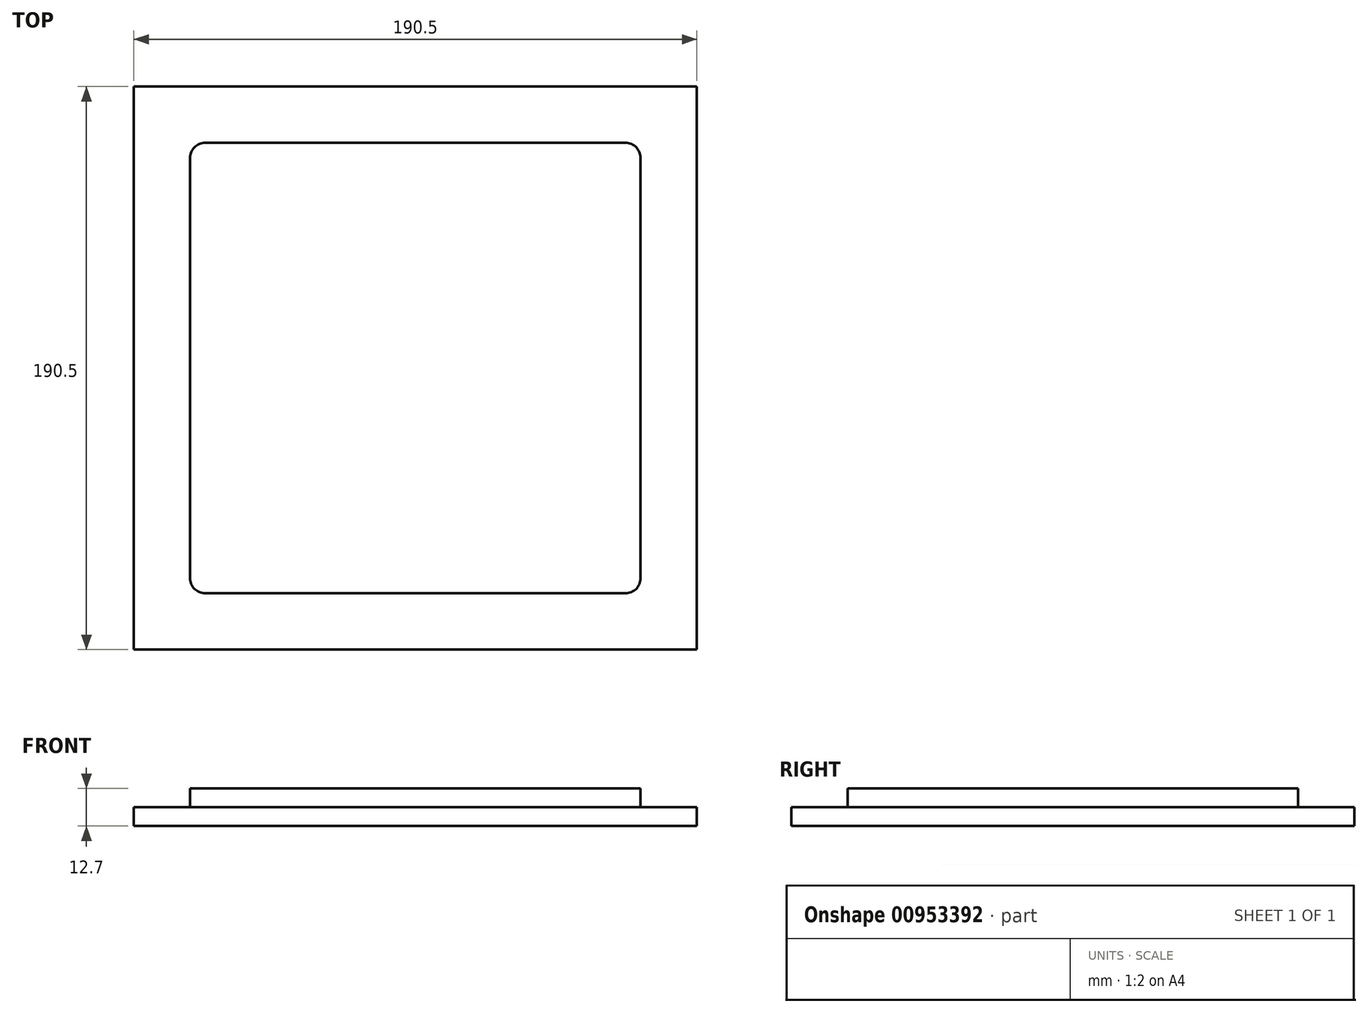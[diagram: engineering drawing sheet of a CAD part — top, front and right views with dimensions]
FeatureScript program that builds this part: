
annotation { "Feature Type Name" : "Feature", "Feature Type Description" : "" }
export const myFeature = defineFeature(function(context is Context, id is Id, definition is map)
    precondition{}
    {
        {
            var Q0;
            Q0=qCreatedBy(makeId("Top.planeOp"),FACE);
            var sketch = newSketch(context, id + "F0", { "sketchPlane" : qUnion([Q0])});
            skLineSegment(sketch, "E0.bottom", {"start": v(-95.25, 95.25) * mm, "end": v(95.25, 95.25) * mm});
            skLineSegment(sketch, "E0.top", {"start": v(-95.25, -95.25) * mm, "end": v(95.25, -95.25) * mm});
            skLineSegment(sketch, "E0.left", {"start": v(-95.25, 95.25) * mm, "end": v(-95.25, -95.25) * mm});
            skLineSegment(sketch, "E0.right", {"start": v(95.25, 95.25) * mm, "end": v(95.25, -95.25) * mm});
            skPoint(sketch, "E0.middle", {"position": v(0, 0) * mm});
            skSolve(sketch);
        }
        {
            var Q0;
            Q0=makeQuery(id+"F0.imprint","IMPRINT",FACE,{"disambiguationData":[TD([[makeQuery(id+"F0.imprint","IMPRINT",EDGE,{"derivedFrom":sQuery(id+"F0.wireOp",EDGE,"E0.bottom")}),-1.0]])]});
            extrude(context, id + "F1", {"entities" : qUnion([Q0]), "depth" : 6.35 * mm, "offsetDistance" : 25.4 * mm});
        }
        {
            var Q0;
            Q0=makeQuery(id+"F1.opExtrude","CAP_FACE",FACE,{"disambiguationData":[OSD([sQuery(id+"F0.wireOp",EDGE,"E0.bottom"),sQuery(id+"F0.wireOp",EDGE,"E0.top"),sQuery(id+"F0.wireOp",EDGE,"E0.left"),sQuery(id+"F0.wireOp",EDGE,"E0.right")])],"isStart":false});
            var sketch = newSketch(context, id + "F2", { "sketchPlane" : qUnion([Q0])});
            skLineSegment(sketch, "E1.bottom", {"start": v(-76.2, 76.2) * mm, "end": v(76.2, 76.2) * mm});
            skLineSegment(sketch, "E1.top", {"start": v(-76.2, -76.2) * mm, "end": v(76.2, -76.2) * mm});
            skLineSegment(sketch, "E1.left", {"start": v(-76.2, 76.2) * mm, "end": v(-76.2, -76.2) * mm});
            skLineSegment(sketch, "E1.right", {"start": v(76.2, 76.2) * mm, "end": v(76.2, -76.2) * mm});
            skPoint(sketch, "E1.middle", {"position": v(0, 0) * mm});
            skSolve(sketch);
        }
        {
            var Q0;
            Q0=makeQuery(id+"F2.imprint","IMPRINT",FACE,{"disambiguationData":[TD([[makeQuery(id+"F2.imprint","IMPRINT",EDGE,{"derivedFrom":sQuery(id+"F2.wireOp",EDGE,"E1.bottom")}),-1.0]])]});
            extrude(context, id + "F3", {"entities" : qUnion([Q0]), "depth" : 6.35 * mm, "offsetDistance" : 25.4 * mm});
        }
        {
            var Q0;
            Q0=makeQuery(id+"F3.opExtrude","SWEPT_EDGE",EDGE,{"disambiguationData":[OSD([sQuery(id+"F2.wireOp",EDGE,"E1.top"),sQuery(id+"F2.wireOp",EDGE,"E1.right")])]});
            var Q1;
            Q1=makeQuery(id+"F3.opExtrude","SWEPT_EDGE",EDGE,{"disambiguationData":[OSD([sQuery(id+"F2.wireOp",EDGE,"E1.top"),sQuery(id+"F2.wireOp",EDGE,"E1.left")])]});
            var Q2;
            Q2=makeQuery(id+"F3.opExtrude","SWEPT_EDGE",EDGE,{"disambiguationData":[OSD([sQuery(id+"F2.wireOp",EDGE,"E1.bottom"),sQuery(id+"F2.wireOp",EDGE,"E1.right")])]});
            var Q3;
            Q3=makeQuery(id+"F3.opExtrude","SWEPT_EDGE",EDGE,{"disambiguationData":[OSD([sQuery(id+"F2.wireOp",EDGE,"E1.bottom"),sQuery(id+"F2.wireOp",EDGE,"E1.left")])]});
            fillet(context, id + "F4", {"entities" : qUnion([Q0, Q1, Q2, Q3]), "radius" : 5.08 * mm, "tangentPropagation" : true, "allowEdgeOverflow" : false});
        }
    });
